# Revit family: FU_Seat_Sandler_Hyppo 6-1
name_source: partatom
category: Furniture
units: mm (PartAtom-declared; Revit-internal decimal feet)

## family parameters
Always vertical = Yes
Cut with Voids When Loaded = No
OmniClass Number = 23.40.20.00
OmniClass Title = General Furniture and Specialties
Room Calculation Point = No
Shared = No
Work Plane-Based = No

## types (1)
- FU_Seat_Sandler_Hyppo 6-1
    Default Elevation = 0 mm  [stored 0 ft]
    Depth = 665 mm  [stored 2.18176 ft]
    Description = Lounge chair with an upholstered seat and back on a solid beech frame, 1 cushion included.
    Height = 730 mm  [stored 2.39501 ft]
    Manufacturer = Sandler
    Model = Hyppo 6.1
    URL = https://www.sandlerseating.com
    Upholstery = Fabric - Manhattan - Lexington YI113
    Width = 770 mm  [stored 2.52625 ft]
    Wood Finish = Wood - Beech - Cherry Wood - V

note: [stored X ft] marks values corroborated as IEEE doubles in the binary element streams (Revit-internal decimal feet)

## geometry (parser evidence)
native form markers: Sweep x4
no freeform markers — native parametric forms only
